# Revit family: Plumbing_Drainage_hansgrohe_RainDrain-Spot-Point-drain-15-x-15-cm-gr___
name_source: partatom
category: Plumbing Fixtures
revit_build: Autodesk Revit 2018 (Build: 20170223_1515(x64)
units: mm (PartAtom-declared; Revit-internal decimal feet)

## family parameters
Cut with Voids When Loaded = No
Host = Face
OmniClass Number = 23.31.17.29
OmniClass Title = Shower Drains
Part Type = Normal
Room Calculation Point = No
Round Connector Dimension = Use Diameter
Shared = No

## types (1)
- 800 Stainless Steel Optic
    Connector Description = Water Outlet 50 mm
    Date Updated = 2023/11/24
    Default Elevation = 1219 mm
    Description = RainDrain Spot Complete set point drain 150/150
    Diameter = 50 mm  [stored 0.164042 ft]
    Edition number = 0
    Manufacturer = Hansgrohe
    Material = Hansgrohe - Metal - 800 Stainless Steel Optic
    Material 1 = Hansgrohe - Plastic - Black
    Model = 56055XXX
    Product Page URL = https://pro.hansgrohe.com
    Product data url = https://bimobject.com
    URL = https://www.hansgrohe.com
    Version = 2

note: [stored X ft] marks values corroborated as IEEE doubles in the binary element streams (Revit-internal decimal feet)

## geometry (parser evidence)
native form markers: Sweep x3
no freeform markers — native parametric forms only
